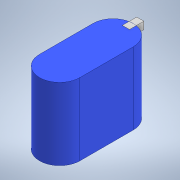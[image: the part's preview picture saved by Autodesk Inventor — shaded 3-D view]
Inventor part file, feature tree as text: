
AUTODESK INVENTOR PART (.ipt)
format: ipt  version: 2020 (Build 240168000, 168)  size: 115,712 bytes
history: native  units: mm
features: extrude x2, sketch x2
ambient origin geometry x8: Origin, YZ Plane, XZ Plane, XY Plane, X Axis, Y Axis, Z Axis, Center Point
bodies: Solid1 (feature_tree), Solid2 (feature_tree)
feature tree (4):
  extrude  "Extrusion1"  Depth=28.0mm
  extrude  "Extrusion2"  Depth=5.0mm
  sketch  "Sketch1"  dims[d0=65.0mm d1=28.0mm]
  sketch  "Sketch2"  dims[d2=50.0mm d3=0.0mm d4=5.0mm d5=10.0mm d6=5.0mm d7=0.1mm d8=0.0mm d9=5.0mm d10=0.0mm]
